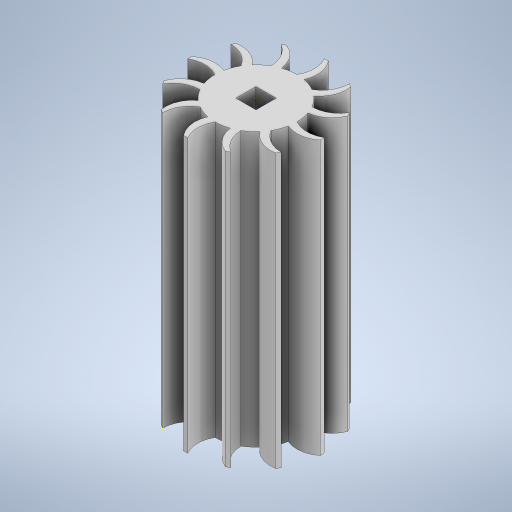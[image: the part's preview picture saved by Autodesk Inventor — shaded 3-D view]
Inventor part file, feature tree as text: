
AUTODESK INVENTOR PART (.ipt)
format: ipt  version: 2023 (Build 270158000, 158)  size: 335,872 bytes
history: native  units: mm
features: sketch x5, extrude x1
ambient origin geometry x8: Origin, YZ Plane, XZ Plane, XY Plane, X Axis, Y Axis, Z Axis, Center Point
bodies: Solid1 (feature_tree)
feature tree (6):
  extrude  "Extrusion1"  Depth=3.0mm
  sketch  "Sketch2"  dims[d2=3.0mm]
  sketch  "Sketch3"  dims[d3=5.0mm]
  sketch  "Sketch4"  dims[d4=5.0mm]
  sketch  "Sketch5"  dims[d5=22.5deg d6=1.963495mm d7=0.981748mm d13=5.0mm d14=120.0mm d16=360.0deg d18=50.0mm d19=0.0mm d20=3.7mm d21=3.7mm]
  sketch  "Sketch1"  dims[d0=15.0mm d1=3.0mm]
